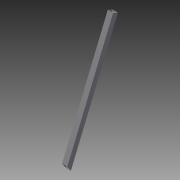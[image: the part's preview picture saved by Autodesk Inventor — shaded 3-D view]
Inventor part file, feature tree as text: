
AUTODESK INVENTOR PART (.ipt)
format: ipt  version: 2013 (Build 170138000, 138)  size: 88,576 bytes
history: native  units: in
note: dims shown in document units (in); Inventor stores cm internally (conversion verified against a paired STEP export)
features: extrude x2, sketch x2
ambient origin geometry x8: Origin, YZ Plane, XZ Plane, XY Plane, X Axis, Y Axis, Z Axis, Center Point
feature tree (4):
  extrude  "Extrusion3"  TaperAngle=90.0deg  [1 undecoded]
  extrude  "Extrusion4"  TaperAngle=22.5deg  [1 undecoded]
  sketch  "Sketch1"  dims[d0=10.0in d1=90.0deg]
  sketch  "Sketch3"  dims[d2=22.5in d3=22.5deg d4=1.0in d5=180.0deg d6=1.0in d7=112.5deg d8=90.0deg d17=1.0in d18=0.0in d19=0.0625in d20=0.0625in d21=0.0625in d22=0.0625in d23=100.0in d24=0.0in]
note: 2 required parameter values undecoded (feature->parameter linkage not recoverable at this tier; creation-order binding heuristic only, values carry confidence <= 0.55)
